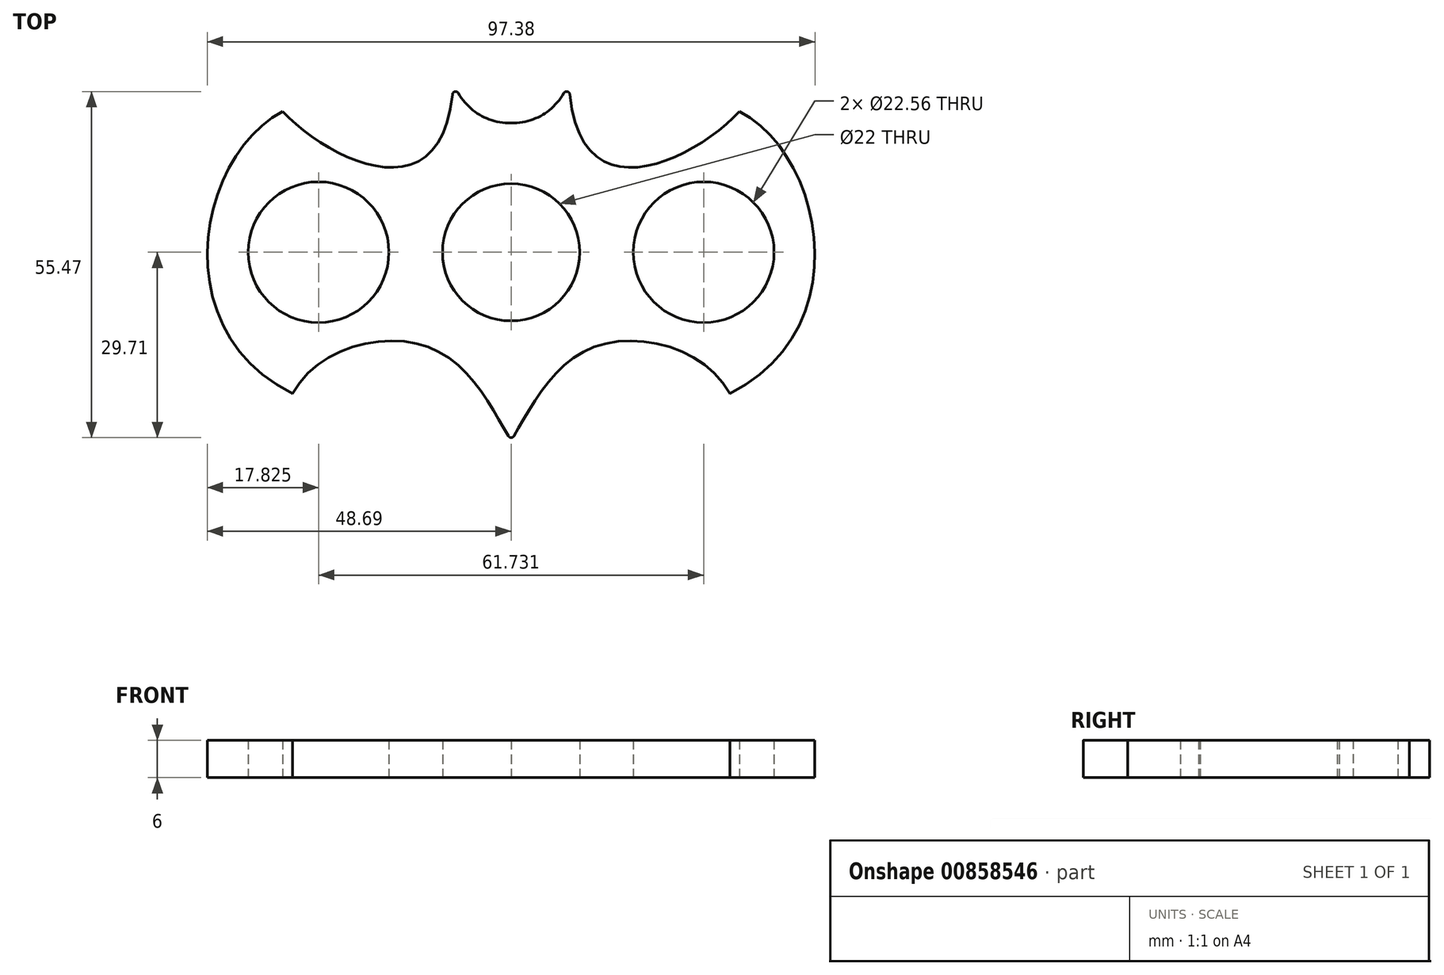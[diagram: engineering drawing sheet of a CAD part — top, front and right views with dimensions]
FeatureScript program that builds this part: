
annotation { "Feature Type Name" : "Feature", "Feature Type Description" : "" }
export const myFeature = defineFeature(function(context is Context, id is Id, definition is map)
    precondition{}
    {
        {
            var Q0;
            Q0=qCreatedBy(makeId("Top.planeOp"),FACE);
            var sketch = newSketch(context, id + "F0", { "sketchPlane" : qUnion([Q0])});
            skCircle(sketch, "E0", {"center": v(0, 0) * mm, "radius": 11 * mm});
            skCircle(sketch, "E1", {"center": v(30.87, 0) * mm, "radius": 11.28 * mm});
            skCircle(sketch, "E2", {"center": v(-30.87, 0) * mm, "radius": 11.28 * mm});
            skFitSpline(sketch, "E3", {"points": [v(0, 20.7) * mm, v(9.27, 27.1) * mm], "startDerivative": vector(12.53, -0.08) * mm, "endDerivative": vector(5.24, 12.4) * mm});
            skFitSpline(sketch, "E4", {"points": [v(9.27, 27.1) * mm, v(36.61, 22.56) * mm], "startDerivative": vector(2.94, -65.43) * mm, "endDerivative": vector(22.52, 23.93) * mm});
            skFitSpline(sketch, "E5", {"points": [v(36.61, 22.56) * mm, v(35.05, -22.65) * mm], "startDerivative": vector(40.58, -21.02) * mm, "endDerivative": vector(-61.93, -30.7) * mm});
            skFitSpline(sketch, "E6", {"points": [v(35.05, -22.65) * mm, v(12.67, -15.44) * mm, v(0, -30.18) * mm], "startDerivative": vector(-23.54, 42.96) * mm, "endDerivative": vector(-16.66, -26.87) * mm});
            skFitSpline(sketch, "E7.MirrorCS", {"points": [v(-35.05, -22.65) * mm, v(-12.67, -15.44) * mm, v(0, -30.18) * mm], "startDerivative": vector(23.54, 42.96) * mm, "endDerivative": vector(16.66, -26.87) * mm});
            skFitSpline(sketch, "E8.MirrorCS", {"points": [v(-36.61, 22.56) * mm, v(-35.05, -22.65) * mm], "startDerivative": vector(-40.58, -21.02) * mm, "endDerivative": vector(61.93, -30.7) * mm});
            skFitSpline(sketch, "E9.MirrorCS", {"points": [v(-9.27, 27.1) * mm, v(-36.61, 22.56) * mm], "startDerivative": vector(-2.94, -65.43) * mm, "endDerivative": vector(-22.52, 23.93) * mm});
            skFitSpline(sketch, "E10.MirrorCS", {"points": [v(0, 20.7) * mm, v(-9.27, 27.1) * mm], "startDerivative": vector(-12.53, -0.08) * mm, "endDerivative": vector(-5.24, 12.4) * mm});
            skSolve(sketch);
        }
        {
            var Q0;
            Q0=makeQuery(id+"F0.imprint","IMPRINT",FACE,{"disambiguationData":[TD([[makeQuery(id+"F0.imprint","IMPRINT",EDGE,{"derivedFrom":sQuery(id+"F0.wireOp",EDGE,"E0")}),-1.0]])]});
            extrude(context, id + "F1", {"entities" : qUnion([Q0]), "endBound" : BoundingType.SYMMETRIC, "depth" : 6 * mm, "offsetDistance" : 25 * mm});
        }
        {
            var Q0;
            Q0=makeQuery(id+"F1.opExtrude","SWEPT_EDGE",EDGE,{"disambiguationData":[OSD([sQuery(id+"F0.wireOp",EDGE,"E9.MirrorCS"),sQuery(id+"F0.wireOp",EDGE,"E10.MirrorCS")])]});
            var Q1;
            Q1=makeQuery(id+"F1.opExtrude","SWEPT_EDGE",EDGE,{"disambiguationData":[OSD([sQuery(id+"F0.wireOp",EDGE,"E3"),sQuery(id+"F0.wireOp",EDGE,"E4")])]});
            var Q2;
            Q2=makeQuery(id+"F1.opExtrude","SWEPT_EDGE",EDGE,{"disambiguationData":[OSD([sQuery(id+"F0.wireOp",EDGE,"E6"),sQuery(id+"F0.wireOp",EDGE,"E7.MirrorCS")])]});
            fillet(context, id + "F2", {"entities" : qUnion([Q0, Q1, Q2]), "radius" : 0.5 * mm, "tangentPropagation" : true, "allowEdgeOverflow" : false});
        }
    });
